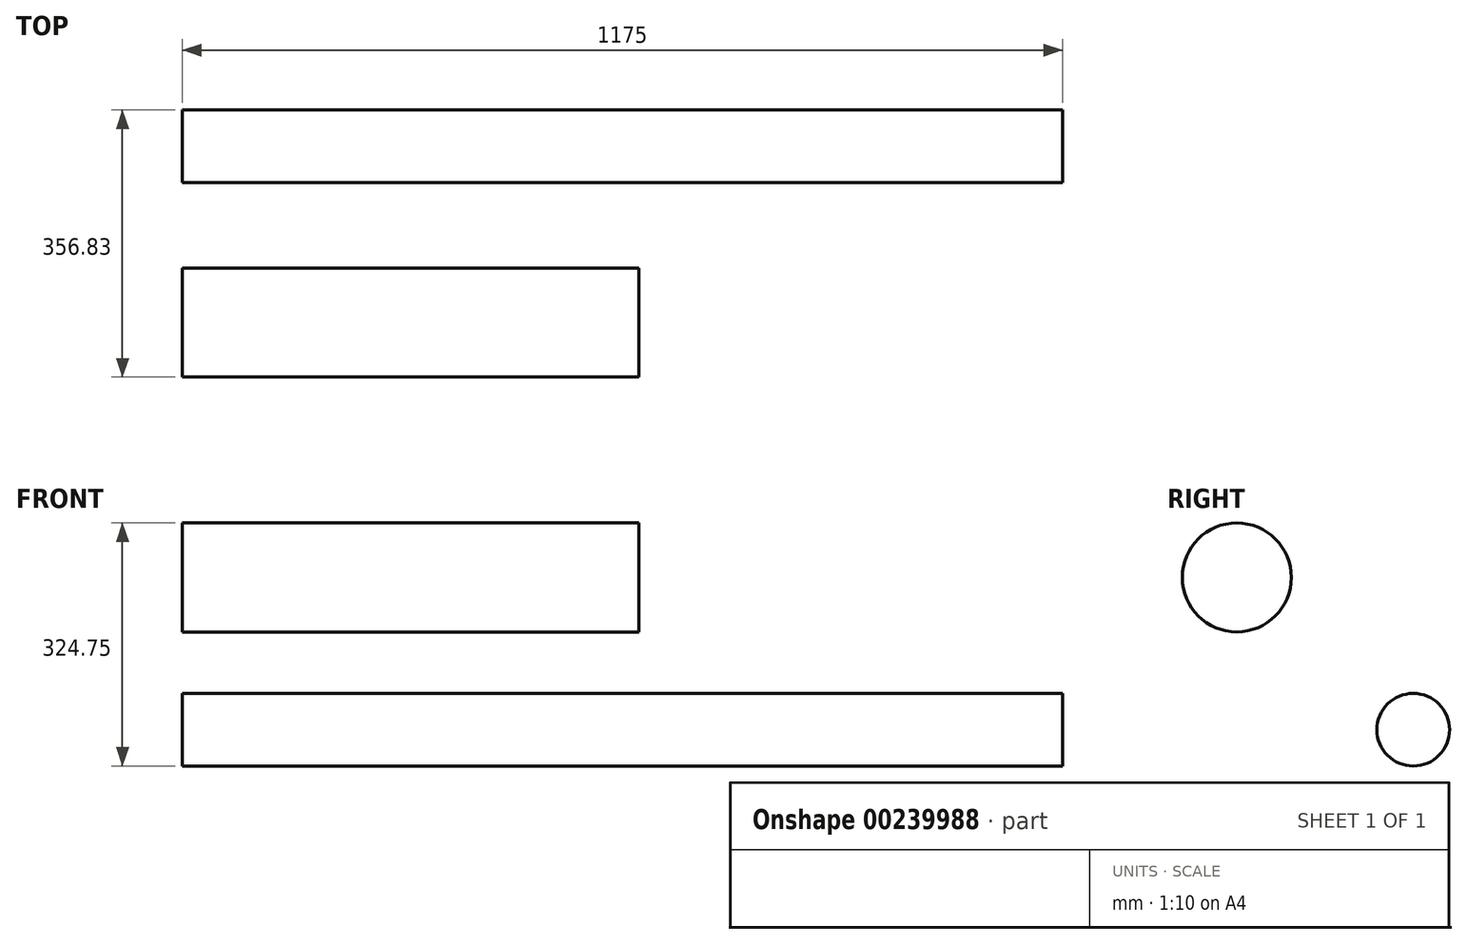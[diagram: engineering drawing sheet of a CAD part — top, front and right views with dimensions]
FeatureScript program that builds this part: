
annotation { "Feature Type Name" : "Feature", "Feature Type Description" : "" }
export const myFeature = defineFeature(function(context is Context, id is Id, definition is map)
    precondition{}
    {
        {
            var Q0;
            Q0=qCreatedBy(makeId("Right.planeOp"),FACE);
            var sketch = newSketch(context, id + "F0", { "sketchPlane" : qUnion([Q0])});
            skCircle(sketch, "E0", {"center": v(-255.76, -53.93) * mm, "radius": 67.78 * mm});
            skCircle(sketch, "E1", {"center": v(172.77, 15.83) * mm, "radius": 48.47 * mm});
            skSolve(sketch);
        }
        {
            var Q0;
            Q0=sQuery(id+"F0.wireOp",EDGE,"E0");
            extrude(context, id + "F1", {"bodyType" : ToolBodyType.SURFACE, "surfaceEntities" : qUnion([Q0]), "depth" : 609.6 * mm});
        }
        {
            var Q0;
            Q0=qCreatedBy(makeId("Right.planeOp"),FACE);
            var sketch = newSketch(context, id + "F2", { "sketchPlane" : qUnion([Q0])});
            skCircle(sketch, "E2", {"center": v(-62.8, 219.31) * mm, "radius": 72.8 * mm});
            skSolve(sketch);
        }
        {
            var Q0;
            Q0=makeQuery(id+"F0.imprint","IMPRINT",FACE,{"disambiguationData":[TD([[makeQuery(id+"F0.imprint","IMPRINT",EDGE,{"derivedFrom":sQuery(id+"F0.wireOp",EDGE,"E1")}),1.0]])]});
            extrude(context, id + "F3", {"entities" : qUnion([Q0]), "depth" : 1175 * mm});
        }
        {
            var Q0;
            Q0=makeQuery(id+"F2.imprint","IMPRINT",FACE,{"disambiguationData":[TD([[makeQuery(id+"F2.imprint","IMPRINT",EDGE,{"derivedFrom":sQuery(id+"F2.wireOp",EDGE,"E2")}),1.0]])]});
            extrude(context, id + "F4", {"entities" : qUnion([Q0]), "depth" : 609.6 * mm});
        }
    });
